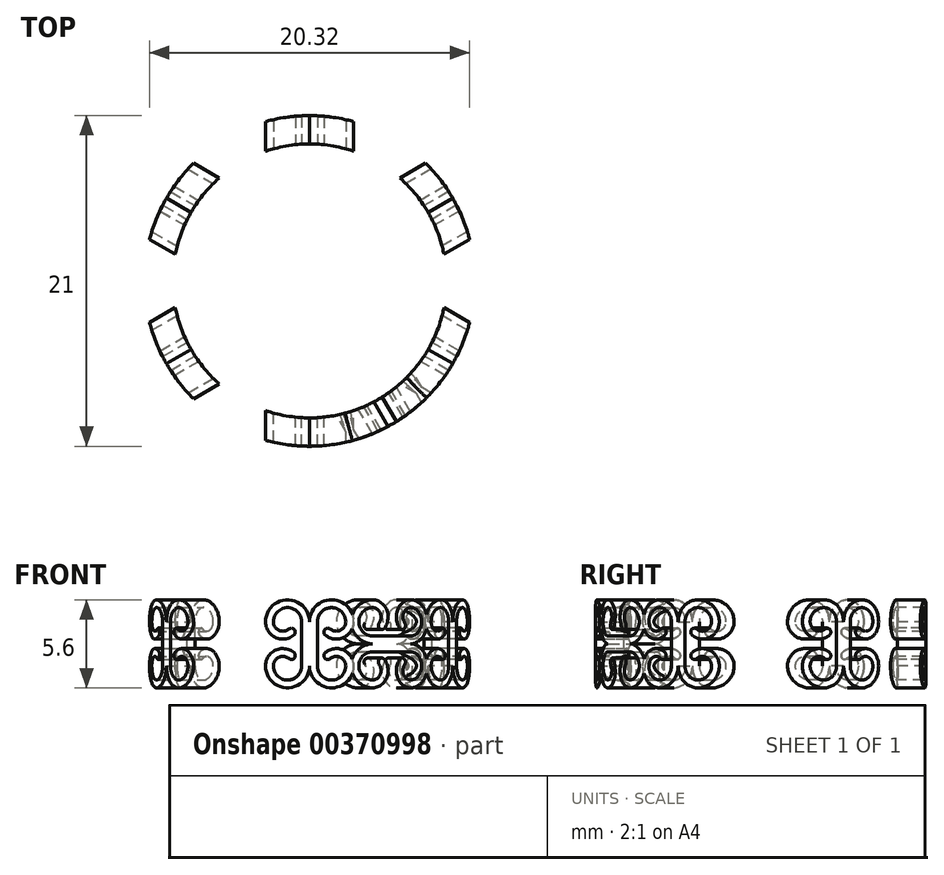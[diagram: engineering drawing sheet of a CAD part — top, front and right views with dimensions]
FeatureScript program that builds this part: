
annotation { "Feature Type Name" : "Feature", "Feature Type Description" : "" }
export const myFeature = defineFeature(function(context is Context, id is Id, definition is map)
    precondition{}
    {
        {
            var Q0;
            Q0=qCreatedBy(makeId("Front.planeOp"),FACE);
            var sketch = newSketch(context, id + "F0", { "sketchPlane" : qUnion([Q0])});
            skLineSegment(sketch, "E0.bottom", {"start": v(0, 0) * mm, "end": v(-2.8, 0) * mm, "construction": true});
            skLineSegment(sketch, "E0.top", {"start": v(0, 2.8) * mm, "end": v(-2.8, 2.8) * mm, "construction": true});
            skLineSegment(sketch, "E0.left", {"start": v(0, 0) * mm, "end": v(0, 2.8) * mm, "construction": true});
            skLineSegment(sketch, "E0.right", {"start": v(-2.8, 0) * mm, "end": v(-2.8, 2.8) * mm, "construction": true});
            skArc(sketch, "E1", {"start": v(0, 1.4) * mm, "mid": v(-1.4, 2.8) * mm, "end": v(-2.8, 1.4) * mm});
            skArc(sketch, "E2", {"start": v(-2.8, 1.4) * mm, "mid": v(-2.16, 0.4) * mm, "end": v(-1, 0.56) * mm});
            skLineSegment(sketch, "E3", {"start": v(-1.7, 1.4) * mm, "end": v(-1, 0.56) * mm, "construction": true});
            skLineSegment(sketch, "E4", {"start": v(-1.7, 1.4) * mm, "end": v(-1.7, 0.3) * mm, "construction": true});
            skArc(sketch, "E5.0", {"start": v(-2.3, 1.4) * mm, "mid": v(-1.95, 0.86) * mm, "end": v(-1.31, 0.94) * mm});
            skArc(sketch, "E5.1", {"start": v(-0.5, 1.4) * mm, "mid": v(-1.4, 2.3) * mm, "end": v(-2.3, 1.4) * mm});
            skArc(sketch, "E6", {"start": v(-1, 0.56) * mm, "mid": v(-0.96, 0.9) * mm, "end": v(-1.31, 0.94) * mm});
            skLineSegment(sketch, "E7", {"start": v(-0.5, 1.4) * mm, "end": v(-0.5, 0) * mm});
            skLineSegment(sketch, "E8", {"start": v(-0.5, 0) * mm, "end": v(0, 0) * mm});
            skLineSegment(sketch, "E9", {"start": v(0, 1.4) * mm, "end": v(0, 0) * mm});
            skLineSegment(sketch, "E10", {"start": v(-0.5, 1.4) * mm, "end": v(0, 1.4) * mm, "construction": true});
            skCircle(sketch, "E11", {"center": v(0, 0) * mm, "radius": 3.3 * mm, "construction": true});
            skSolve(sketch);
        }
        {
            var Q0;
            Q0=makeQuery(id+"F0.imprint","IMPRINT",FACE,{"disambiguationData":[TD([[makeQuery(id+"F0.imprint","IMPRINT",EDGE,{"derivedFrom":sQuery(id+"F0.wireOp",EDGE,"E1")}),1.0]])]});
            extrude(context, id + "F1", {"entities" : qUnion([Q0]), "endBound" : BoundingType.SYMMETRIC, "depth" : 8 * mm});
        }
        {
            var Q0;
            Q0=makeQuery(id+"F1.opExtrude","SWEPT_BODY",BODY,{"disambiguationData":[OSD([sQuery(id+"F0.wireOp",EDGE,"E1"),sQuery(id+"F0.wireOp",EDGE,"E2"),sQuery(id+"F0.wireOp",EDGE,"E5.0"),sQuery(id+"F0.wireOp",EDGE,"E5.1"),sQuery(id+"F0.wireOp",EDGE,"E6"),sQuery(id+"F0.wireOp",EDGE,"E7"),sQuery(id+"F0.wireOp",EDGE,"E8"),sQuery(id+"F0.wireOp",EDGE,"E9")])]});
            var Q1;
            Q1=makeQuery(id+"F1.opExtrude","SWEPT_FACE",FACE,{"disambiguationData":[OSD([sQuery(id+"F0.wireOp",EDGE,"E8")])]});
            mirror(context, id + "F2", {"operationType" : NewBodyOperationType.ADD, "entities" : qUnion([Q0]), "mirrorPlane" : qUnion([Q1])});
        }
        {
            var Q0;
            Q0=makeQuery(id+"F1.opExtrude","SWEPT_BODY",BODY,{"disambiguationData":[OSD([sQuery(id+"F0.wireOp",EDGE,"E1"),sQuery(id+"F0.wireOp",EDGE,"E2"),sQuery(id+"F0.wireOp",EDGE,"E5.0"),sQuery(id+"F0.wireOp",EDGE,"E5.1"),sQuery(id+"F0.wireOp",EDGE,"E6"),sQuery(id+"F0.wireOp",EDGE,"E7"),sQuery(id+"F0.wireOp",EDGE,"E8"),sQuery(id+"F0.wireOp",EDGE,"E9")])]});
            var Q1;
            {var subQ0=makeQuery(id+"F1.opExtrude","SWEPT_FACE",FACE,{"disambiguationData":[OSD([sQuery(id+"F0.wireOp",EDGE,"E9")])]});Q1=makeQuery(id+"F2.boolean.opBoolean","MERGE",FACE,{"derivedFrom":[subQ0,makeQuery(id+"F2.opPattern","COPY",FACE,{"derivedFrom":subQ0,"instanceName":"1"})]});}
            mirror(context, id + "F3", {"operationType" : NewBodyOperationType.ADD, "entities" : qUnion([Q0]), "mirrorPlane" : qUnion([Q1])});
        }
        {
            var Q0;
            Q0=qCreatedBy(makeId("Top.planeOp"),FACE);
            var sketch = newSketch(context, id + "F4", { "sketchPlane" : qUnion([Q0])});
            skCircle(sketch, "E12", {"center": v(0, 11) * mm, "radius": 11 * mm, "construction": true});
            skSolve(sketch);
        }
        {
            var Q0;
            Q0=makeQuery(id+"F1.opExtrude","SWEPT_BODY",BODY,{"disambiguationData":[OSD([sQuery(id+"F0.wireOp",EDGE,"E1"),sQuery(id+"F0.wireOp",EDGE,"E2"),sQuery(id+"F0.wireOp",EDGE,"E5.0"),sQuery(id+"F0.wireOp",EDGE,"E5.1"),sQuery(id+"F0.wireOp",EDGE,"E6"),sQuery(id+"F0.wireOp",EDGE,"E7"),sQuery(id+"F0.wireOp",EDGE,"E8"),sQuery(id+"F0.wireOp",EDGE,"E9")])]});
            var Q1;
            Q1=sQuery(id+"F0.wireOp",EDGE,"E11");
            transform(context, id + "F5", {"entities" : qUnion([Q0]), "transformType" : TransformType.ROTATION, "transformAxis" : qUnion([Q1]), "angle" : 90 * degree, "makeCopy" : true});
        }
        {
            var Q0;
            Q0=makeQuery(id+"F5.opPattern","COPY",BODY,{"derivedFrom":makeQuery(id+"F1.opExtrude","SWEPT_BODY",BODY,{"disambiguationData":[OSD([sQuery(id+"F0.wireOp",EDGE,"E1"),sQuery(id+"F0.wireOp",EDGE,"E2"),sQuery(id+"F0.wireOp",EDGE,"E5.0"),sQuery(id+"F0.wireOp",EDGE,"E5.1"),sQuery(id+"F0.wireOp",EDGE,"E6"),sQuery(id+"F0.wireOp",EDGE,"E7"),sQuery(id+"F0.wireOp",EDGE,"E8"),sQuery(id+"F0.wireOp",EDGE,"E9")])]}),"instanceName":"1"});
            var Q1;
            Q1=sQuery(id+"F4.wireOp",EDGE,"E12");
            transform(context, id + "F6", {"entities" : qUnion([Q0]), "transformType" : TransformType.ROTATION, "transformAxis" : qUnion([Q1]), "angle" : 30 * degree, "makeCopy" : false});
        }
        {
            var Q0;
            Q0=qCreatedBy(makeId("Top.planeOp"),FACE);
            var sketch = newSketch(context, id + "F7", { "sketchPlane" : qUnion([Q0])});
            skCircle(sketch, "E13.0", {"center": v(0, 11) * mm, "radius": 8.7 * mm});
            skCircle(sketch, "E14", {"center": v(0, 11) * mm, "radius": 10.5 * mm});
            skCircle(sketch, "E15", {"center": v(0, 11) * mm, "radius": 50 * mm});
            skSolve(sketch);
        }
        {
            var Q0;
            Q0=makeQuery(id+"F7.imprint","IMPRINT",FACE,{"disambiguationData":[TD([[makeQuery(id+"F7.imprint","IMPRINT",EDGE,{"derivedFrom":sQuery(id+"F7.wireOp",EDGE,"E14")}),-1.0]])]});
            var Q1;
            Q1=makeQuery(id+"F7.imprint","IMPRINT",FACE,{"disambiguationData":[TD([[makeQuery(id+"F7.imprint","IMPRINT",EDGE,{"derivedFrom":sQuery(id+"F7.wireOp",EDGE,"E13.0")}),1.0]])]});
            extrude(context, id + "F8", {"entities" : qUnion([Q0, Q1]), "operationType" : NewBodyOperationType.REMOVE, "endBound" : BoundingType.SYMMETRIC, "oppositeDirection" : true, "depth" : 50 * mm});
        }
        {
            var Q0;
            Q0=makeQuery(id+"F1.opExtrude","SWEPT_BODY",BODY,{"disambiguationData":[OSD([sQuery(id+"F0.wireOp",EDGE,"E1"),sQuery(id+"F0.wireOp",EDGE,"E2"),sQuery(id+"F0.wireOp",EDGE,"E5.0"),sQuery(id+"F0.wireOp",EDGE,"E5.1"),sQuery(id+"F0.wireOp",EDGE,"E6"),sQuery(id+"F0.wireOp",EDGE,"E7"),sQuery(id+"F0.wireOp",EDGE,"E8"),sQuery(id+"F0.wireOp",EDGE,"E9")])]});
            var Q1;
            Q1=sQuery(id+"F4.wireOp",EDGE,"E12");
            circularPattern(context, id + "F9", {"operationType" : NewBodyOperationType.ADD, "entities" : qUnion([Q0]), "axis" : qUnion([Q1]), "angle" : 360 * degree, "instanceCount" : 6, "equalSpace" : true});
        }
    });
